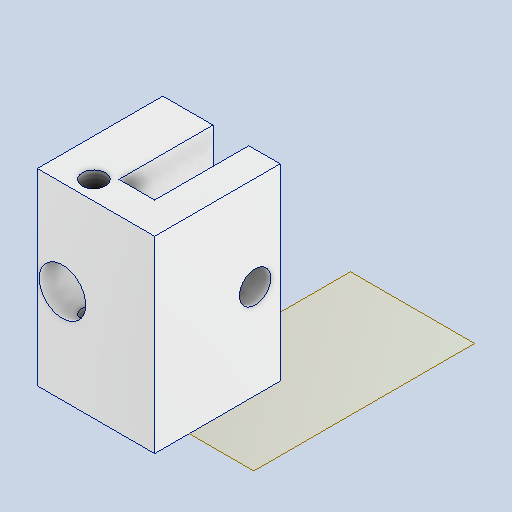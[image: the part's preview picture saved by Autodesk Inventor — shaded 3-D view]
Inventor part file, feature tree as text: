
AUTODESK INVENTOR PART (.ipt)
format: ipt  version: 2025 (Build 290162010, 162A)  size: 262,656 bytes
history: native  units: mm
features: sketch x9, hole x8, projected_geometry x4, other x3, plane x1, extrude x1, thread x1, reference x1
ambient origin geometry x8: Origin, YZ Plane, XZ Plane, XY Plane, X Axis, Y Axis, Z Axis, Center Point
bodies: Volumenkörper1 (feature_tree)
feature tree (28):
  plane  "Arbeitsebene1"
  extrude  "Extrusion1"  Depth=30.0mm TaperAngle=0.0deg
  hole  "GLHU"  [1 undecoded]
  hole  "GLHH"  [1 undecoded]
  hole  "GLHO"  [1 undecoded]
  hole  "DLHO"  [1 undecoded]
  hole  "DLHU"  [1 undecoded]
  hole  "Zentrierbolzen"  [1 undecoded]
  hole  "LK-Verschraubung"  [1 undecoded]
  hole  "seiloese"  [1 undecoded]
  thread  "Gewinde4"  [1 undecoded]
  sketch  "Skizze1"  dims[d0=5.0mm d1=8.0mm d2=5.0mm d3=20.0mm d4=2.1mm d5=30.0mm d6=0.0mm]
  reference  "Referenz1"
  sketch  "Skizze3"  dims[d15=1.567mm d16=2.5mm d17=4.0mm d18=2.0mm d19=90.0deg d20=4.0mm d21=20.594885mm d42=2.5mm]
  sketch  "Skizze6"  dims[d43=3.0mm]
  projected_geometry  "Projizierte Kontur5"
  sketch  "Skizze8"  dims[d44=2.0mm d45=6.0mm d46=4.0mm d47=2.0mm d48=90.0deg d49=5.0mm d50=20.594885mm d58=4.0mm]
  projected_geometry  "Projizierte Kontur7"
  sketch  "Skizze9"  dims[d59=4.0mm d60=6.0mm d61=7.4mm d62=14.0mm d63=90.0deg d64=8.0mm d65=20.594885mm]
  projected_geometry  "Projizierte Kontur8"
  sketch  "Skizze10"  dims[d66=1.567mm d67=2.5mm d68=4.0mm d69=2.0mm d70=90.0deg d71=4.0mm d72=20.594885mm d74=9.0mm]
  sketch  "Skizze11"  dims[d75=4.0mm]
  projected_geometry  "Projizierte Kontur9"
  sketch  "Skizze12"  dims[d76=1.567mm d77=2.5mm d78=4.0mm d79=2.0mm d80=90.0deg d81=4.0mm d82=20.594885mm]
  sketch  "Skizze13"  dims[d83=5.0mm d84=2.5mm d85=4.0mm d86=2.0mm d87=90.0deg d88=4.0mm d89=20.594885mm d90=5.0mm d91=6.0mm d92=7.4mm d93=11.0mm d94=90.0deg d95=8.0mm d96=20.594885mm d100=3.688101mm d101=9.0mm d102=4.0mm d103=2.0mm d104=90.0deg d105=8.0mm d106=20.594885mm d107=9.0mm d108=0.0mm d109=6.0mm d110=3.0mm d97=1.0mm d98=1.0mm d99=1.0mm]
  other  "<userpath>\Documents\Inventor\Krandemonstrator\Demonstrator.iam"
  other  "Demonstrator.iam"
  other  "Träger:1"
note: 9 required parameter values undecoded (feature->parameter linkage not recoverable at this tier; creation-order binding heuristic only, values carry confidence <= 0.55)
